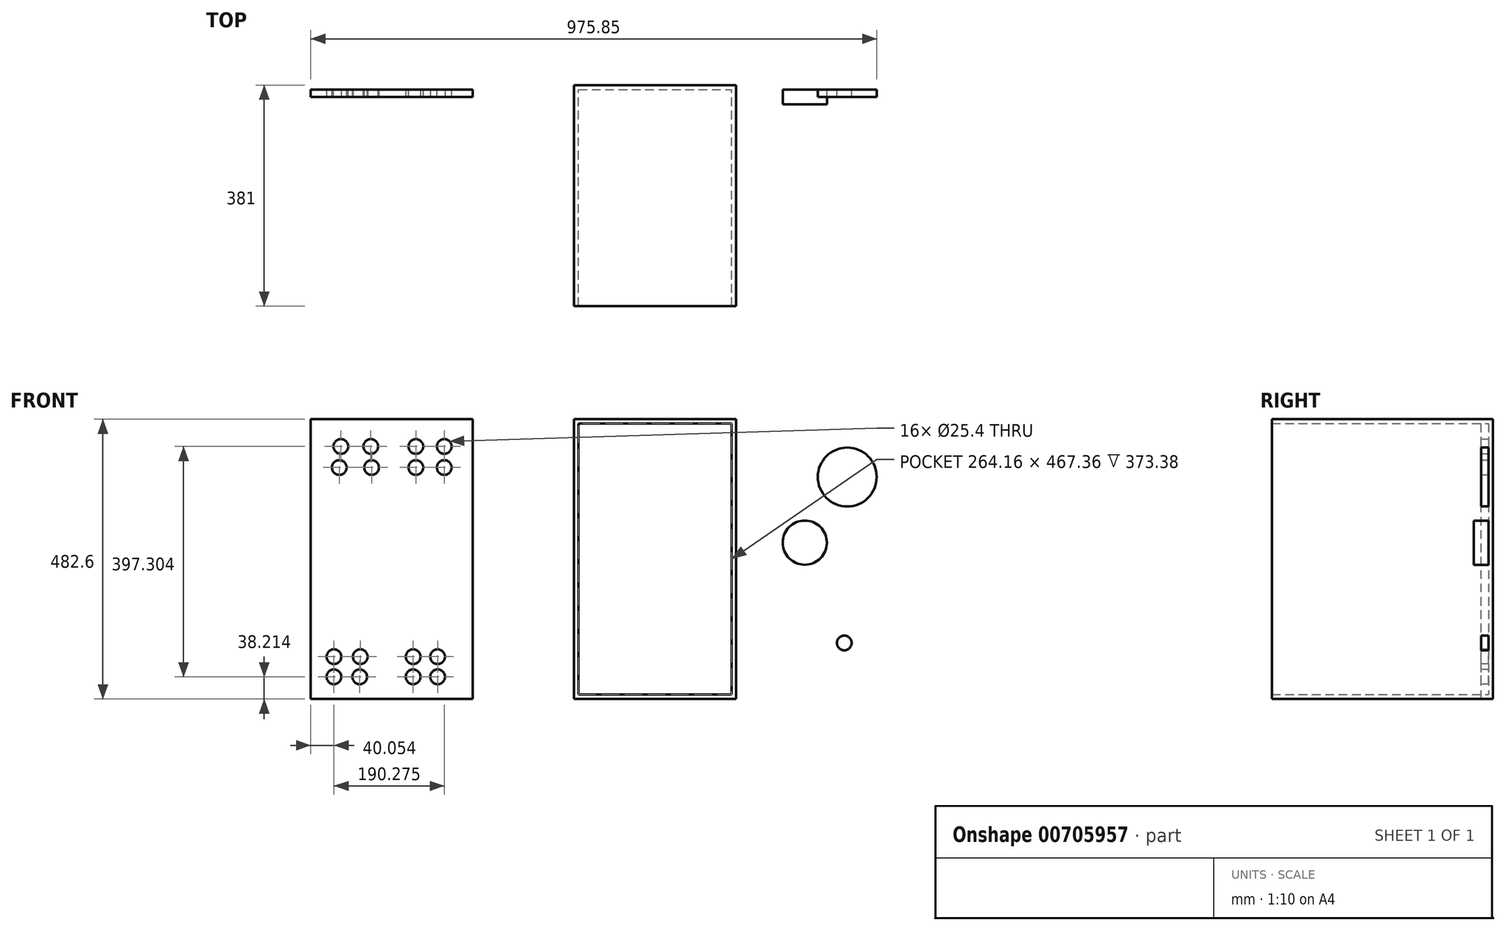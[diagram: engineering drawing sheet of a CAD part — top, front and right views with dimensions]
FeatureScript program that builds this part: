
annotation { "Feature Type Name" : "Feature", "Feature Type Description" : "" }
export const myFeature = defineFeature(function(context is Context, id is Id, definition is map)
    precondition{}
    {
        {
            var Q0;
            Q0=qCreatedBy(makeId("Front.planeOp"),FACE);
            var sketch = newSketch(context, id + "F0", { "sketchPlane" : qUnion([Q0])});
            skLineSegment(sketch, "E0.bottom", {"start": v(-139.7, 241.3) * mm, "end": v(139.7, 241.3) * mm});
            skLineSegment(sketch, "E0.top", {"start": v(-139.7, -241.3) * mm, "end": v(139.7, -241.3) * mm});
            skLineSegment(sketch, "E0.left", {"start": v(-139.7, 241.3) * mm, "end": v(-139.7, -241.3) * mm});
            skLineSegment(sketch, "E0.right", {"start": v(139.7, 241.3) * mm, "end": v(139.7, -241.3) * mm});
            skPoint(sketch, "E0.middle", {"position": v(0, 0) * mm});
            skSolve(sketch);
        }
        {
            var Q0;
            Q0 = qSketchRegion(id + "F0", true);
            extrude(context, id + "F1", {"entities" : qUnion([Q0]), "depth" : 381 * mm, "offsetDistance" : 25.4 * mm});
        }
        {
            var Q0;
            Q0=makeQuery(id+"F1.opExtrude","CAP_FACE",FACE,{"disambiguationData":[OSD([sQuery(id+"F0.wireOp",EDGE,"E0.bottom"),sQuery(id+"F0.wireOp",EDGE,"E0.top"),sQuery(id+"F0.wireOp",EDGE,"E0.left"),sQuery(id+"F0.wireOp",EDGE,"E0.right")])],"isStart":false});
            shell(context, id + "F2", {"entities" : qUnion([Q0]), "thickness" : 7.62 * mm});
        }
        {
            var Q0;
            Q0=makeQuery(id+"F2.opShell","OFFSET_FACE",FACE,{"disambiguationData":[OSD([sQuery(id+"F0.wireOp",EDGE,"E0.bottom"),sQuery(id+"F0.wireOp",EDGE,"E0.top"),sQuery(id+"F0.wireOp",EDGE,"E0.left"),sQuery(id+"F0.wireOp",EDGE,"E0.right")])]});
            var sketch = newSketch(context, id + "F3", { "sketchPlane" : qUnion([Q0])});
            skLineSegment(sketch, "E1.bottom", {"start": v(-314.5, -241.3) * mm, "end": v(-593.9, -241.3) * mm});
            skLineSegment(sketch, "E1.top", {"start": v(-314.5, 241.3) * mm, "end": v(-593.9, 241.3) * mm});
            skLineSegment(sketch, "E1.left", {"start": v(-314.5, -241.3) * mm, "end": v(-314.5, 241.3) * mm});
            skLineSegment(sketch, "E1.right", {"start": v(-593.9, -241.3) * mm, "end": v(-593.9, 241.3) * mm});
            skPoint(sketch, "E1.middle", {"position": v(-454.2, 0) * mm});
            skSolve(sketch);
        }
        {
            var Q0;
            Q0=makeQuery(id+"F3.imprint","IMPRINT",FACE,{"disambiguationData":[TD([[makeQuery(id+"F3.imprint","IMPRINT",EDGE,{"derivedFrom":sQuery(id+"F3.wireOp",EDGE,"E1.bottom")}),-1.0]])]});
            extrude(context, id + "F4", {"entities" : qUnion([Q0]), "depth" : 12.7 * mm, "offsetDistance" : 25.4 * mm});
        }
        {
            var Q0;
            Q0=makeQuery(id+"F2.opShell","OFFSET_FACE",FACE,{"disambiguationData":[OSD([sQuery(id+"F0.wireOp",EDGE,"E0.bottom"),sQuery(id+"F0.wireOp",EDGE,"E0.top"),sQuery(id+"F0.wireOp",EDGE,"E0.left"),sQuery(id+"F0.wireOp",EDGE,"E0.right")])]});
            var sketch = newSketch(context, id + "F5", { "sketchPlane" : qUnion([Q0])});
            skCircle(sketch, "E2", {"center": v(257.97, 28.26) * mm, "radius": 38.1 * mm});
            skCircle(sketch, "E3", {"center": v(245.6, 190.42) * mm, "radius": 50.8 * mm});
            skSolve(sketch);
        }
        {
            var Q0;
            Q0=makeQuery(id+"F5.imprint","IMPRINT",FACE,{"disambiguationData":[TD([[makeQuery(id+"F5.imprint","IMPRINT",EDGE,{"derivedFrom":sQuery(id+"F5.wireOp",EDGE,"E2")}),1.0]])]});
            extrude(context, id + "F6", {"entities" : qUnion([Q0]), "depth" : 25.4 * mm, "offsetDistance" : 25.4 * mm});
        }
        {
            var Q0;
            Q0=makeQuery(id+"F2.opShell","OFFSET_FACE",FACE,{"disambiguationData":[OSD([sQuery(id+"F0.wireOp",EDGE,"E0.bottom"),sQuery(id+"F0.wireOp",EDGE,"E0.top"),sQuery(id+"F0.wireOp",EDGE,"E0.left"),sQuery(id+"F0.wireOp",EDGE,"E0.right")])]});
            var sketch = newSketch(context, id + "F7", { "sketchPlane" : qUnion([Q0])});
            skCircle(sketch, "E4", {"center": v(331.15, 141.54) * mm, "radius": 50.8 * mm});
            skSolve(sketch);
        }
        {
            var Q0;
            Q0=makeQuery(id+"F7.imprint","IMPRINT",FACE,{"disambiguationData":[TD([[makeQuery(id+"F7.imprint","IMPRINT",EDGE,{"derivedFrom":sQuery(id+"F7.wireOp",EDGE,"E4")}),1.0]])]});
            extrude(context, id + "F8", {"entities" : qUnion([Q0]), "depth" : 12.7 * mm, "offsetDistance" : 25.4 * mm});
        }
        {
            var Q0;
            Q0=makeQuery(id+"F2.opShell","OFFSET_FACE",FACE,{"disambiguationData":[OSD([sQuery(id+"F0.wireOp",EDGE,"E0.bottom"),sQuery(id+"F0.wireOp",EDGE,"E0.top"),sQuery(id+"F0.wireOp",EDGE,"E0.left"),sQuery(id+"F0.wireOp",EDGE,"E0.right")])]});
            var sketch = newSketch(context, id + "F9", { "sketchPlane" : qUnion([Q0])});
            skCircle(sketch, "E5", {"center": v(325.97, -144.65) * mm, "radius": 12.7 * mm});
            skSolve(sketch);
        }
        {
            var Q0;
            Q0=makeQuery(id+"F9.imprint","IMPRINT",FACE,{"disambiguationData":[TD([[makeQuery(id+"F9.imprint","IMPRINT",EDGE,{"derivedFrom":sQuery(id+"F9.wireOp",EDGE,"E5")}),1.0]])]});
            extrude(context, id + "F10", {"entities" : qUnion([Q0]), "depth" : 12.7 * mm, "offsetDistance" : 25.4 * mm});
        }
        {
            var Q0;
            Q0=makeQuery(id+"F4.opExtrude","CAP_FACE",FACE,{"disambiguationData":[OSD([sQuery(id+"F3.wireOp",EDGE,"E1.bottom"),sQuery(id+"F3.wireOp",EDGE,"E1.top"),sQuery(id+"F3.wireOp",EDGE,"E1.left"),sQuery(id+"F3.wireOp",EDGE,"E1.right")])],"isStart":true});
            var sketch = newSketch(context, id + "F11", { "sketchPlane" : qUnion([Q0])});
            skCircle(sketch, "E6", {"center": v(363.57, 194.22) * mm, "radius": 12.7 * mm});
            skCircle(sketch, "E7", {"center": v(412.62, 194.22) * mm, "radius": 12.7 * mm});
            skCircle(sketch, "E8", {"center": v(363.57, 157.9) * mm, "radius": 12.7 * mm});
            skCircle(sketch, "E9", {"center": v(412.62, 157.9) * mm, "radius": 12.7 * mm});
            skCircle(sketch, "E10", {"center": v(490.4, 194.22) * mm, "radius": 12.7 * mm});
            skCircle(sketch, "E11", {"center": v(541.93, 194.22) * mm, "radius": 12.7 * mm});
            skCircle(sketch, "E12", {"center": v(488.85, 157.9) * mm, "radius": 12.7 * mm});
            skCircle(sketch, "E13", {"center": v(544.57, 157.9) * mm, "radius": 12.7 * mm});
            skSolve(sketch);
        }
        {
            var Q0;
            Q0=sQuery(id+"F11.wireOp",VERTEX,"E6.center");
            var Q1;
            Q1=sQuery(id+"F11.wireOp",VERTEX,"E7.center");
            var Q2;
            Q2=sQuery(id+"F11.wireOp",VERTEX,"E9.center");
            var Q3;
            Q3=sQuery(id+"F11.wireOp",VERTEX,"E8.center");
            var Q4;
            Q4=sQuery(id+"F11.wireOp",VERTEX,"E12.center");
            var Q5;
            Q5=sQuery(id+"F11.wireOp",VERTEX,"E13.center");
            var Q6;
            Q6=sQuery(id+"F11.wireOp",VERTEX,"E11.center");
            var Q7;
            Q7=sQuery(id+"F11.wireOp",VERTEX,"E10.center");
            var Q8;
            Q8=makeQuery(id+"F4.opExtrude","SWEPT_BODY",BODY,{"disambiguationData":[OSD([sQuery(id+"F3.wireOp",EDGE,"E1.bottom"),sQuery(id+"F3.wireOp",EDGE,"E1.top"),sQuery(id+"F3.wireOp",EDGE,"E1.left"),sQuery(id+"F3.wireOp",EDGE,"E1.right")])]});
            hole(context, id + "F12", {"style" : HoleStyle.SIMPLE, "endStyle" : HoleEndStyle.THROUGH, "holeDiameter" : 25.4 * mm, "majorDiameter" : 6.35 * mm, "isTappedThrough" : true, "tappedDepth" : 12.7 * mm, "tapClearance" : 3, "locations" : qUnion([Q0, Q1, Q2, Q3, Q4, Q5, Q6, Q7]), "scope" : qUnion([Q8])});
        }
        {
            var Q0;
            Q0=makeQuery(id+"F4.opExtrude","CAP_FACE",FACE,{"disambiguationData":[OSD([sQuery(id+"F3.wireOp",EDGE,"E1.bottom"),sQuery(id+"F3.wireOp",EDGE,"E1.top"),sQuery(id+"F3.wireOp",EDGE,"E1.left"),sQuery(id+"F3.wireOp",EDGE,"E1.right")])],"isStart":false});
            var sketch = newSketch(context, id + "F13", { "sketchPlane" : qUnion([Q0])});
            skCircle(sketch, "E14", {"center": v(-553.85, -203.09) * mm, "radius": 12.7 * mm});
            skCircle(sketch, "E15", {"center": v(-553.85, -168.43) * mm, "radius": 12.7 * mm});
            skCircle(sketch, "E16", {"center": v(-508.35, -168.43) * mm, "radius": 12.7 * mm});
            skCircle(sketch, "E17", {"center": v(-509.44, -203.09) * mm, "radius": 12.7 * mm});
            skCircle(sketch, "E18", {"center": v(-417.37, -168.43) * mm, "radius": 12.7 * mm});
            skCircle(sketch, "E19", {"center": v(-417.37, -203.09) * mm, "radius": 12.7 * mm});
            skCircle(sketch, "E20", {"center": v(-375.13, -203.09) * mm, "radius": 12.7 * mm});
            skCircle(sketch, "E21", {"center": v(-375.13, -168.43) * mm, "radius": 12.7 * mm});
            skSolve(sketch);
        }
        {
            var Q0;
            Q0=sQuery(id+"F13.wireOp",VERTEX,"E16.center");
            var Q1;
            Q1=sQuery(id+"F13.wireOp",VERTEX,"E15.center");
            var Q2;
            Q2=sQuery(id+"F13.wireOp",VERTEX,"E14.center");
            var Q3;
            Q3=sQuery(id+"F13.wireOp",VERTEX,"E17.center");
            var Q4;
            Q4=sQuery(id+"F13.wireOp",VERTEX,"E19.center");
            var Q5;
            Q5=sQuery(id+"F13.wireOp",VERTEX,"E20.center");
            var Q6;
            Q6=sQuery(id+"F13.wireOp",VERTEX,"E18.center");
            var Q7;
            Q7=sQuery(id+"F13.wireOp",VERTEX,"E21.center");
            var Q8;
            Q8=makeQuery(id+"F4.opExtrude","SWEPT_BODY",BODY,{"disambiguationData":[OSD([sQuery(id+"F3.wireOp",EDGE,"E1.bottom"),sQuery(id+"F3.wireOp",EDGE,"E1.top"),sQuery(id+"F3.wireOp",EDGE,"E1.left"),sQuery(id+"F3.wireOp",EDGE,"E1.right")])]});
            hole(context, id + "F14", {"style" : HoleStyle.SIMPLE, "endStyle" : HoleEndStyle.THROUGH, "holeDiameter" : 25.4 * mm, "majorDiameter" : 6.35 * mm, "isTappedThrough" : true, "tappedDepth" : 12.7 * mm, "tapClearance" : 3, "locations" : qUnion([Q0, Q1, Q2, Q3, Q4, Q5, Q6, Q7]), "scope" : qUnion([Q8])});
        }
    });
